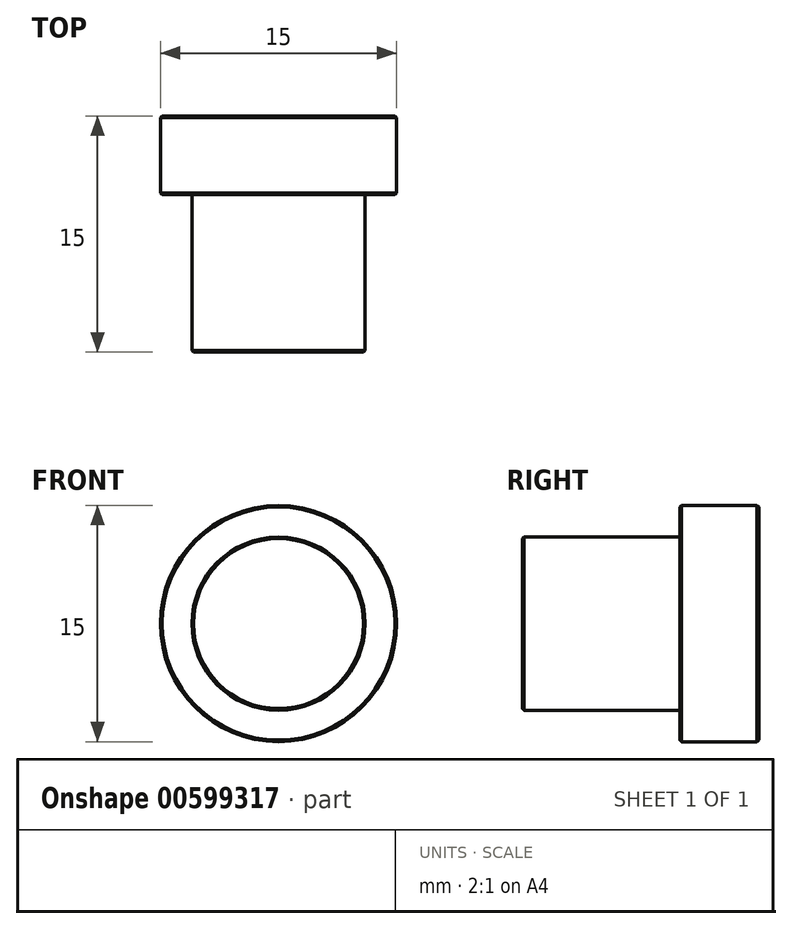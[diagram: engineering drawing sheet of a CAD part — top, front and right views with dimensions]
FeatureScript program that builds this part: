
annotation { "Feature Type Name" : "Feature", "Feature Type Description" : "" }
export const myFeature = defineFeature(function(context is Context, id is Id, definition is map)
    precondition{}
    {
        {
            var Q0;
            Q0=qCreatedBy(makeId("Front.planeOp"),FACE);
            var sketch = newSketch(context, id + "F0", { "sketchPlane" : qUnion([Q0])});
            skCircle(sketch, "E0", {"center": v(0, 0) * mm, "radius": 5.5 * mm});
            skCircle(sketch, "E1", {"center": v(0, 0) * mm, "radius": 7.5 * mm});
            skSolve(sketch);
        }
        {
            var Q0;
            Q0=makeQuery(id+"F0.imprint","IMPRINT",FACE,{"disambiguationData":[TD([[makeQuery(id+"F0.imprint","IMPRINT",EDGE,{"derivedFrom":sQuery(id+"F0.wireOp",EDGE,"E0")}),-1.0]])]});
            var Q1;
            Q1=makeQuery(id+"F0.imprint","IMPRINT",FACE,{"disambiguationData":[TD([[makeQuery(id+"F0.imprint","IMPRINT",EDGE,{"derivedFrom":sQuery(id+"F0.wireOp",EDGE,"E0")}),1.0]])]});
            extrude(context, id + "F1", {"entities" : qUnion([Q0, Q1]), "oppositeDirection" : true, "depth" : 5 * mm, "offsetDistance" : 25 * mm});
        }
        {
            var Q0;
            Q0=makeQuery(id+"F0.imprint","IMPRINT",FACE,{"disambiguationData":[TD([[makeQuery(id+"F0.imprint","IMPRINT",EDGE,{"derivedFrom":sQuery(id+"F0.wireOp",EDGE,"E0")}),1.0]])]});
            extrude(context, id + "F2", {"entities" : qUnion([Q0]), "operationType" : NewBodyOperationType.ADD, "depth" : 10 * mm, "offsetDistance" : 25 * mm});
        }
        {
            var Q0;
            Q0=makeQuery(id+"F2.opExtrude","CAP_FACE",FACE,{"disambiguationData":[OSD([sQuery(id+"F0.wireOp",EDGE,"E0")])],"isStart":false});
            var Q1;
            Q1=makeQuery(id+"F1.opExtrude","SWEPT_FACE",FACE,{"disambiguationData":[OSD([sQuery(id+"F0.wireOp",EDGE,"E1")])]});
            chamfer(context, id + "F3", {"entities" : qUnion([Q0, Q1]), "width" : .1 * mm, "tangentPropagation" : true});
        }
    });
